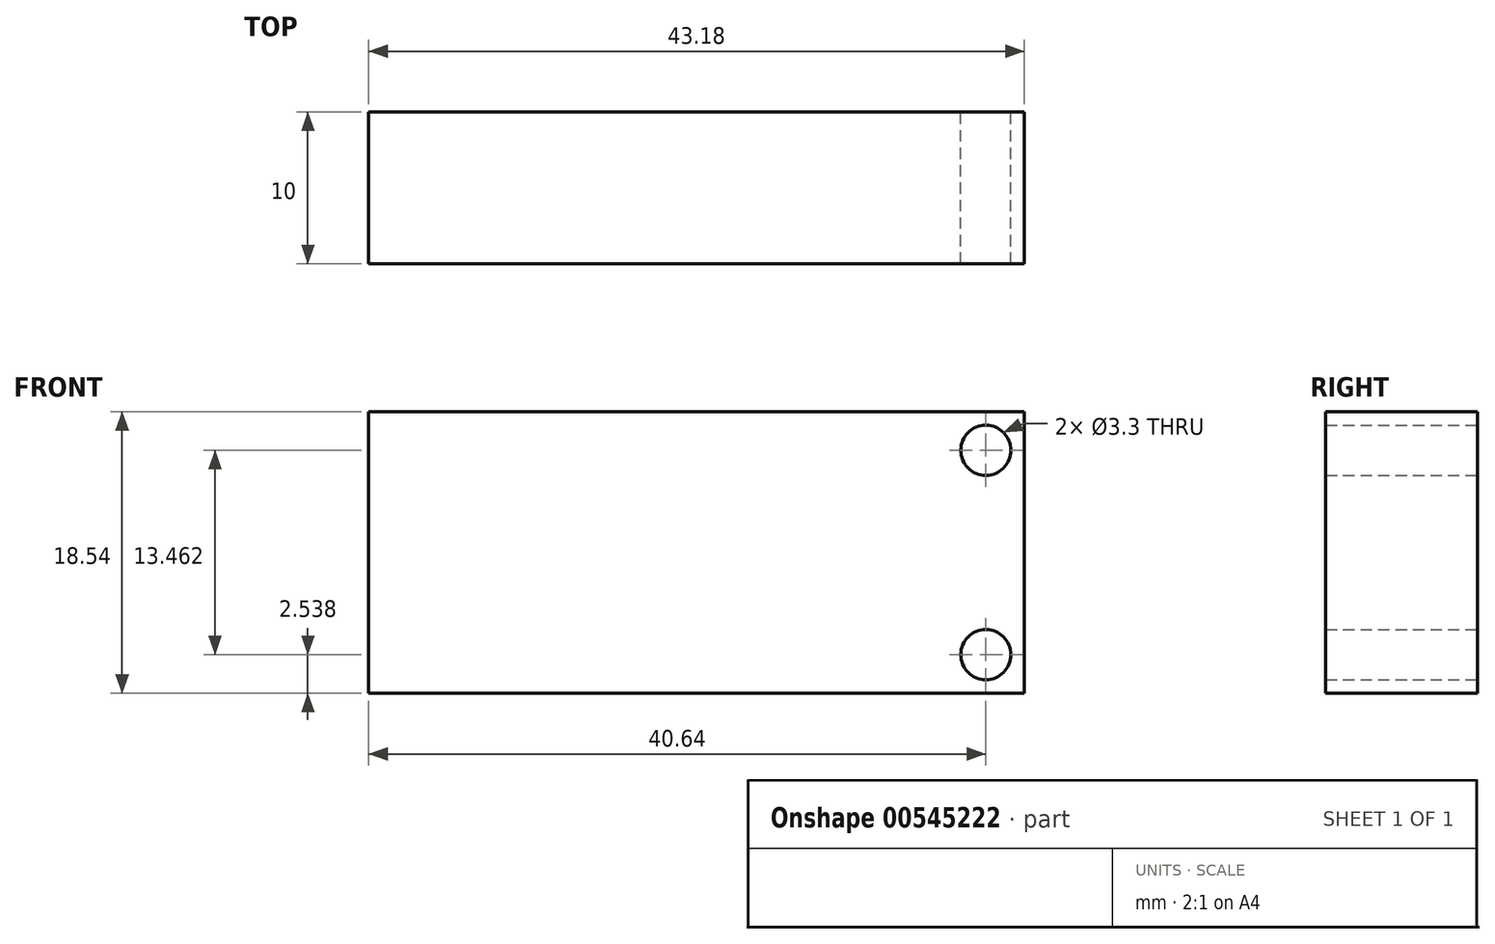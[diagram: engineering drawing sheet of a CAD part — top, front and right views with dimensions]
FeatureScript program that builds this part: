
annotation { "Feature Type Name" : "Feature", "Feature Type Description" : "" }
export const myFeature = defineFeature(function(context is Context, id is Id, definition is map)
    precondition{}
    {
        {
            var Q0;
            Q0=qCreatedBy(makeId("Front.planeOp"),FACE);
            var sketch = newSketch(context, id + "F0", { "sketchPlane" : qUnion([Q0])});
            skLineSegment(sketch, "E0.bottom", {"start": v(-43.18, -18.54) * mm, "end": v(0, -18.54) * mm});
            skLineSegment(sketch, "E0.top", {"start": v(-43.18, 0) * mm, "end": v(0, 0) * mm});
            skLineSegment(sketch, "E0.left", {"start": v(-43.18, -18.54) * mm, "end": v(-43.18, 0) * mm});
            skLineSegment(sketch, "E0.right", {"start": v(0, -18.54) * mm, "end": v(0, 0) * mm});
            skCircle(sketch, "E1", {"center": v(-2.54, -2.54) * mm, "radius": 1.65 * mm});
            skCircle(sketch, "E2", {"center": v(-2.54, -16) * mm, "radius": 1.65 * mm});
            skSolve(sketch);
        }
        {
            var Q0;
            Q0=makeQuery(id+"F0.imprint","IMPRINT",FACE,{"disambiguationData":[TD([[makeQuery(id+"F0.imprint","IMPRINT",EDGE,{"derivedFrom":sQuery(id+"F0.wireOp",EDGE,"E0.bottom")}),1.0]])]});
            extrude(context, id + "F1", {"entities" : qUnion([Q0]), "depth" : 10 * mm, "offsetDistance" : 25.4 * mm});
        }
    });
